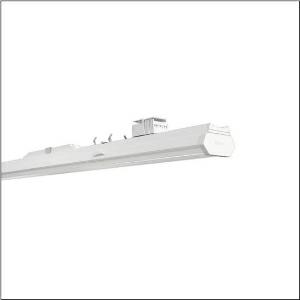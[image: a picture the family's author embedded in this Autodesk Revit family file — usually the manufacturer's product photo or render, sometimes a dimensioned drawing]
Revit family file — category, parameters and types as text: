
# Revit family: licross_r__21_performance_ho_52td16mn4e5m_6ed4
name_source: partatom
category: Lighting Fixtures
units: mm (PartAtom-declared; Revit-internal decimal feet)

## family parameters
Cut with Voids When Loaded = No
Host = Face
Light Source = No
Part Type = Normal
Room Calculation Point = No
Round Connector Dimension = Use Diameter
Shared = No

## types (1)
- --- (1 x LED, 14970 lm, 83.2 W, 4000K)
    Apparent Load = 83 VA
    CIE Flux Codes = 63 87 95 78 100
    Color Rendering = 80
    Color Temperature = 4000K
    Default Elevation = 1800 mm
    Description = Licross® 21 Performance HO, luminaire insert, of sheet steel, galvanised, coil coated, white, length: 1.500mm, width: 120mm, height: 123mm, LED rated luminous flux: 14.970lm, light colour: 840, control gear: ON/OFF Multilumen, control gear: ECG Multilumen, with plug, 3-pole, with phase selection, mains connection: 220..240V, AC, 50/60Hz, halogen-free wiring, primary light control with lens, of plastic, primary optical cover: cover, of PMMA, light emission: direct/indirect distribution, primary light characteristic: symmetric, protection rating (complete): IP54, insulation class (complete): insulation class I (protective earthing), certification: CE, ENEC, UKCA, protection symbol: D if used in an environment with non-conductive dust loads with corresponding accessories, impact resistance: IK06, permissible ambient temperature for indoor applications: -35..+35°C, corresponds to IFS (International Featured Standards) requirements for safety and quality in the food industry, reducing of maximum allowable ambient temperature of 5°C with ceiling mounting, LABS conformity tested according to VDMA 24364:2018-05, packaging unit: 1 piece
    Height = 114 mm
    Lamp = 1 x LED
    Lamp Light Flux = 14970 lm
    Lamp Power = 83.2 W
    Lamp count = 1
    Length = 1500 mm
    Luminous efficacy = 180 lm/W
    Manufacturer = Siteco
    ModVariant = No
    Model = 52TD16MN4E5M
    Mounting Place = Ceiling
    Mounting Type = Pendant
    Number of Poles = 1
    OnlyDefault = Yes
    Power Factor = 1
    Product Name = Licross® 21 Performance HO
    Product group = luminaire insert
    ProductGroupID = 902
    Protection Class = Protection class I
    Protection Degree = IP 54
    RLX_Detail_Level = 1
    RlxData = <blob elided: 29537 chars, md5=b2c2e7c4>
    Socket = socket
    Standby Power = 0 W
    System Light Flux = 14970 lm
    System Power = 83 W
    Type Comments = factory setting: luminous flux: 100 % | (A | C | E) | 195 mA
    Type Image = l_1256148.jpg
    URL = http://relux.com
    VarID = @adj_017703
    Voltage = 0 V
    Weight = 0.00 kg
    Width = 120 mm

## geometry (parser evidence)
native form markers: Blend x4, Sweep x13
no freeform markers — native parametric forms only
